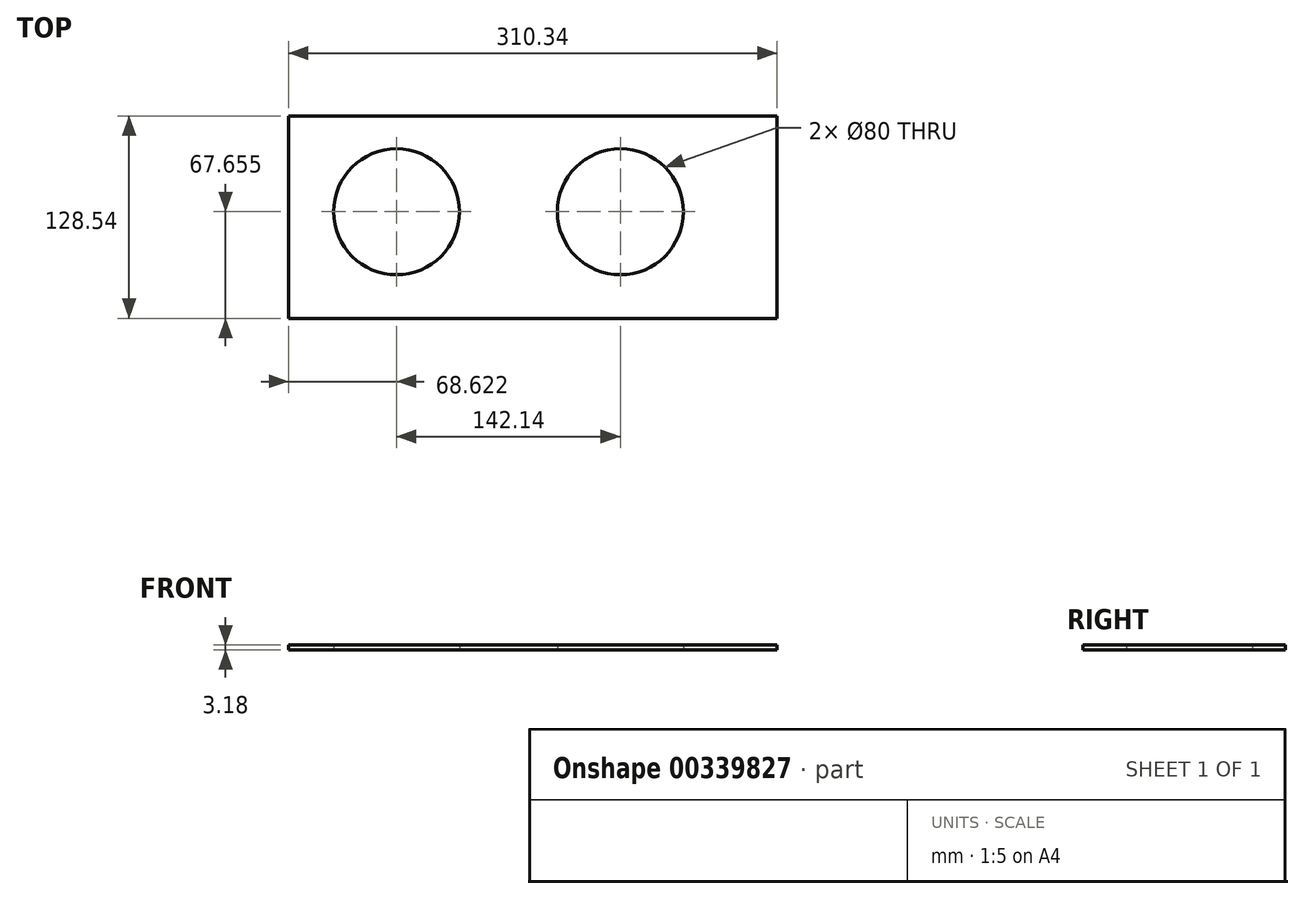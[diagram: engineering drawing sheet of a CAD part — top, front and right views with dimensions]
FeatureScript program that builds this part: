
annotation { "Feature Type Name" : "Feature", "Feature Type Description" : "" }
export const myFeature = defineFeature(function(context is Context, id is Id, definition is map)
    precondition{}
    {
        {
            var Q0;
            Q0=qCreatedBy(makeId("Top.planeOp"),FACE);
            var sketch = newSketch(context, id + "F0", { "sketchPlane" : qUnion([Q0])});
            skLineSegment(sketch, "E0.bottom", {"start": v(-149.1, -18.26) * mm, "end": v(161.25, -18.26) * mm});
            skLineSegment(sketch, "E0.top", {"start": v(-149.1, 110.28) * mm, "end": v(161.25, 110.28) * mm});
            skLineSegment(sketch, "E0.left", {"start": v(-149.1, -18.26) * mm, "end": v(-149.1, 110.28) * mm});
            skLineSegment(sketch, "E0.right", {"start": v(161.25, -18.26) * mm, "end": v(161.25, 110.28) * mm});
            skSolve(sketch);
        }
        {
            var Q0;
            Q0=makeQuery(id+"F0.imprint","IMPRINT",FACE,{"disambiguationData":[TD([[makeQuery(id+"F0.imprint","IMPRINT",EDGE,{"derivedFrom":sQuery(id+"F0.wireOp",EDGE,"E0.bottom")}),1.0]])]});
            var sketch = newSketch(context, id + "F1", { "sketchPlane" : qUnion([Q0])});
            skCircle(sketch, "E1", {"center": v(-80.47, 49.4) * mm, "radius": 40 * mm});
            skLineSegment(sketch, "E2.bottom", {"start": v(-125.47, 94.4) * mm, "end": v(-35.47, 94.4) * mm, "construction": true});
            skLineSegment(sketch, "E2.top", {"start": v(-125.47, 4.4) * mm, "end": v(-35.47, 4.4) * mm, "construction": true});
            skLineSegment(sketch, "E2.left", {"start": v(-125.47, 94.4) * mm, "end": v(-125.47, 4.4) * mm, "construction": true});
            skLineSegment(sketch, "E2.right", {"start": v(-35.47, 94.4) * mm, "end": v(-35.47, 4.4) * mm, "construction": true});
            skLineSegment(sketch, "E3", {"start": v(-125.47, 49.4) * mm, "end": v(-35.47, 49.4) * mm, "construction": true});
            skPoint(sketch, "E4", {"position": v(-125.47, 94.4) * mm});
            skPoint(sketch, "E5", {"position": v(-125.47, 4.4) * mm});
            skPoint(sketch, "E6", {"position": v(-35.47, 4.4) * mm});
            skPoint(sketch, "E7", {"position": v(-35.47, 94.4) * mm});
            skSolve(sketch);
        }
        {
            var Q0;
            Q0=makeQuery(id+"F1.imprint","IMPRINT",FACE,{"disambiguationData":[TD([[makeQuery(id+"F1.imprint","IMPRINT",EDGE,{"derivedFrom":sQuery(id+"F1.wireOp",EDGE,"E1")}),-1.0]])]});
            var sketch = newSketch(context, id + "F2", { "sketchPlane" : qUnion([Q0])});
            skSolve(sketch);
        }
        {
            var Q0;
            Q0=makeQuery(id+"F1.imprint","IMPRINT",FACE,{"disambiguationData":[TD([[makeQuery(id+"F1.imprint","IMPRINT",EDGE,{"derivedFrom":sQuery(id+"F1.wireOp",EDGE,"E1")}),-1.0]])]});
            extrude(context, id + "F3", {"entities" : qUnion([Q0]), "depth" : 3.17 * mm});
        }
        {
            var Q0;
            Q0=makeQuery(id+"F2.imprint","IMPRINT",FACE,{"disambiguationData":[TD([[makeQuery(id+"F2.imprint","IMPRINT",EDGE,{"derivedFrom":makeQuery(id+"F1.imprint","IMPRINT",EDGE,{"derivedFrom":sQuery(id+"F1.wireOp",EDGE,"E1")})}),-1.0]])]});
            var sketch = newSketch(context, id + "F4", { "sketchPlane" : qUnion([Q0])});
            skLineSegment(sketch, "E8.bottom", {"start": v(16.67, 94.4) * mm, "end": v(106.67, 94.4) * mm, "construction": true});
            skLineSegment(sketch, "E8.top", {"start": v(16.67, 4.4) * mm, "end": v(106.67, 4.4) * mm, "construction": true});
            skLineSegment(sketch, "E8.left", {"start": v(16.67, 94.4) * mm, "end": v(16.67, 4.4) * mm, "construction": true});
            skLineSegment(sketch, "E8.right", {"start": v(106.67, 94.4) * mm, "end": v(106.67, 4.4) * mm, "construction": true});
            skLineSegment(sketch, "E9", {"start": v(-35.47, 49.4) * mm, "end": v(16.67, 49.4) * mm, "construction": true});
            skLineSegment(sketch, "E10", {"start": v(16.67, 49.4) * mm, "end": v(106.67, 49.4) * mm, "construction": true});
            skCircle(sketch, "E11", {"center": v(61.67, 49.4) * mm, "radius": 40 * mm});
            skSolve(sketch);
        }
        {
            var Q0;
            Q0=makeQuery(id+"F4.imprint","IMPRINT",FACE,{"disambiguationData":[TD([[makeQuery(id+"F4.imprint","IMPRINT",EDGE,{"derivedFrom":sQuery(id+"F4.wireOp",EDGE,"E11")}),1.0]])]});
            var Q1;
            Q1=sQuery(id+"F4.wireOp",EDGE,"E11");
            extrude(context, id + "F5", {"entities" : qUnion([Q0]), "operationType" : NewBodyOperationType.REMOVE, "surfaceEntities" : qUnion([Q1]), "depth" : 25.4 * mm});
        }
    });
